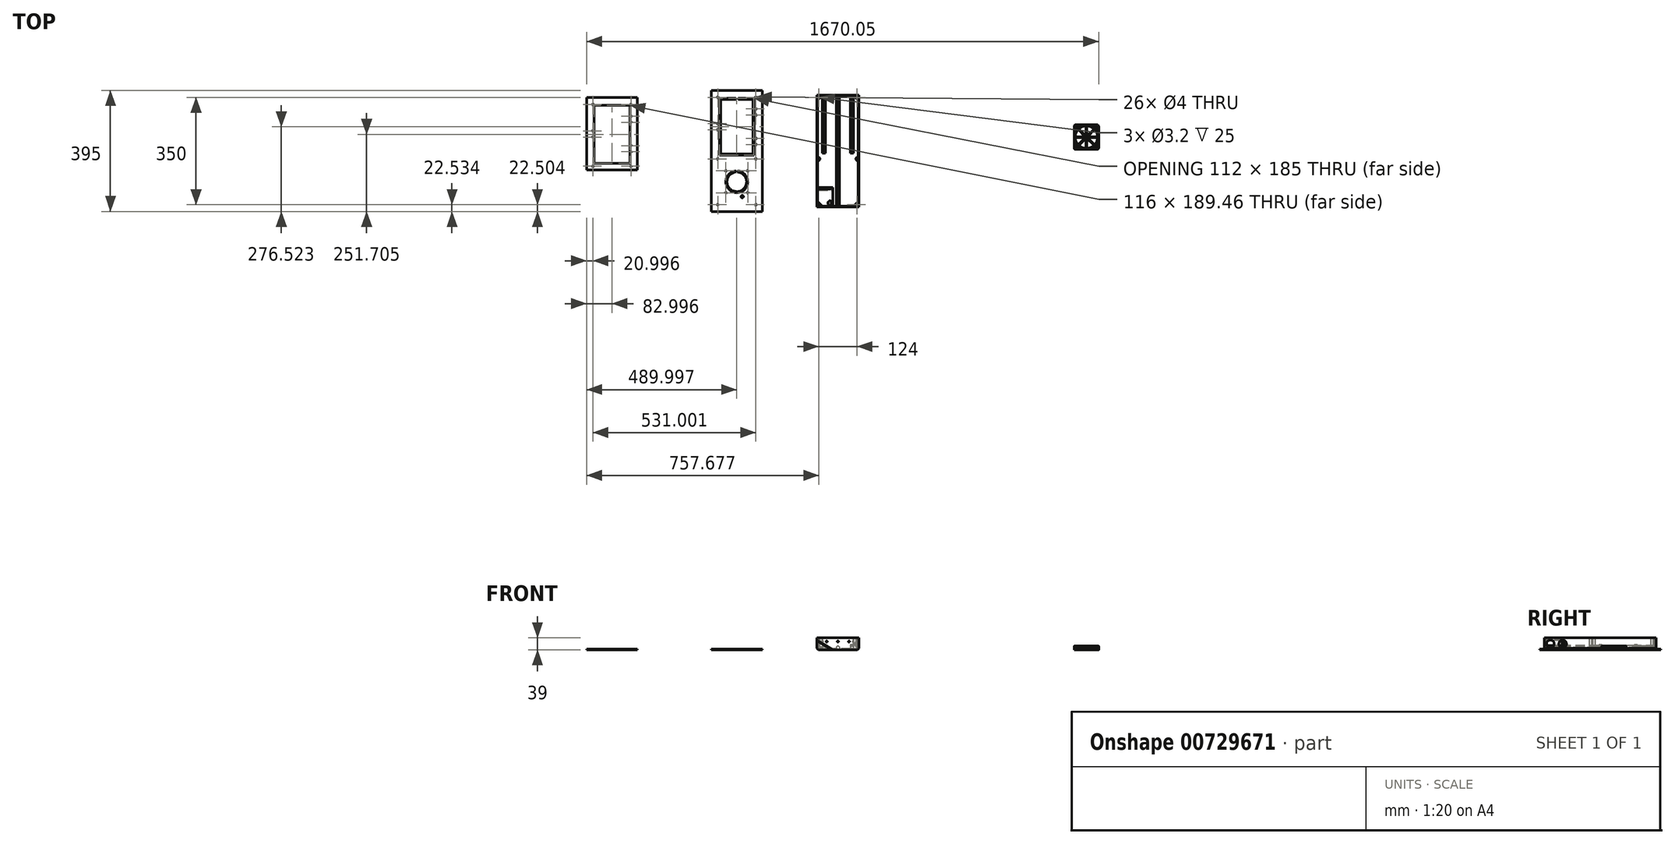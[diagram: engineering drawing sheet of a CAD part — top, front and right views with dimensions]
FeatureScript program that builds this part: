
annotation { "Feature Type Name" : "Feature", "Feature Type Description" : "" }
export const myFeature = defineFeature(function(context is Context, id is Id, definition is map)
    precondition{}
    {
        {
            var Q0;
            Q0=qCreatedBy(makeId("Top.planeOp"),FACE);
            var sketch = newSketch(context, id + "F0", { "sketchPlane" : qUnion([Q0])});
            skLineSegment(sketch, "E0.bottom", {"start": v(-453.37, 96.62) * mm, "end": v(-317.37, 96.62) * mm});
            skLineSegment(sketch, "E0.top", {"start": v(-453.37, -268.38) * mm, "end": v(-317.37, -268.38) * mm});
            skLineSegment(sketch, "E0.left", {"start": v(-453.37, 96.62) * mm, "end": v(-453.37, -268.38) * mm});
            skLineSegment(sketch, "E0.right", {"start": v(-317.37, 96.62) * mm, "end": v(-317.37, -268.38) * mm});
            skSolve(sketch);
        }
        {
            var Q0;
            Q0 = qSketchRegion(id + "F0", true);
            extrude(context, id + "F1", {"entities" : qUnion([Q0]), "depth" : 4 * mm, "offsetDistance" : 25 * mm});
        }
        {
            var Q0;
            Q0=makeQuery(id+"F1.opExtrude","CAP_FACE",FACE,{"disambiguationData":[OSD([sQuery(id+"F0.wireOp",EDGE,"E0.bottom"),sQuery(id+"F0.wireOp",EDGE,"E0.top"),sQuery(id+"F0.wireOp",EDGE,"E0.left"),sQuery(id+"F0.wireOp",EDGE,"E0.right")])],"isStart":false});
            var sketch = newSketch(context, id + "F2", { "sketchPlane" : qUnion([Q0])});
            skLineSegment(sketch, "E1.bottom", {"start": v(-453.37, 96.62) * mm, "end": v(-317.37, 96.62) * mm});
            skLineSegment(sketch, "E1.top", {"start": v(-453.37, -268.38) * mm, "end": v(-317.37, -268.38) * mm});
            skLineSegment(sketch, "E1.left", {"start": v(-453.37, 96.62) * mm, "end": v(-453.37, -268.38) * mm});
            skLineSegment(sketch, "E1.right", {"start": v(-317.37, 96.62) * mm, "end": v(-317.37, -268.38) * mm});
            skLineSegment(sketch, "E2.bottom", {"start": v(-319.87, -265.88) * mm, "end": v(-450.87, -265.88) * mm});
            skLineSegment(sketch, "E2.top", {"start": v(-319.87, 94.12) * mm, "end": v(-450.87, 94.12) * mm});
            skLineSegment(sketch, "E2.left", {"start": v(-319.87, -265.88) * mm, "end": v(-319.87, 94.12) * mm});
            skLineSegment(sketch, "E2.right", {"start": v(-450.87, -265.88) * mm, "end": v(-450.87, 94.12) * mm});
            skPoint(sketch, "E2.middle", {"position": v(-385.37, -85.88) * mm});
            skPoint(sketch, "E2.middle.positionSnap0", {"position": v(-385.37, 96.62) * mm});
            skPoint(sketch, "E2.middle.positionSnap1", {"position": v(-453.37, -85.88) * mm});
            skPoint(sketch, "E2.centerSnap0", {"position": v(-385.37, 96.62) * mm});
            skPoint(sketch, "E2.centerSnap1", {"position": v(-453.37, -85.88) * mm});
            skSolve(sketch);
        }
        {
            var Q0;
            Q0 = qSketchRegion(id + "F2", true);
            extrude(context, id + "F3", {"entities" : qUnion([Q0]), "operationType" : NewBodyOperationType.ADD, "depth" : 35 * mm, "offsetDistance" : 25 * mm});
        }
        {
            var Q0;
            Q0=makeQuery(id+"F1.opExtrude","CAP_FACE",FACE,{"disambiguationData":[OSD([sQuery(id+"F0.wireOp",EDGE,"E0.bottom"),sQuery(id+"F0.wireOp",EDGE,"E0.top"),sQuery(id+"F0.wireOp",EDGE,"E0.left"),sQuery(id+"F0.wireOp",EDGE,"E0.right")])],"isStart":false});
            var sketch = newSketch(context, id + "F4", { "sketchPlane" : qUnion([Q0])});
            skLineSegment(sketch, "E3", {"start": v(-385.37, 94.12) * mm, "end": v(-385.37, -265.88) * mm, "construction": true});
            skLineSegment(sketch, "E4.bottom", {"start": v(-450.87, 94.12) * mm, "end": v(-319.87, 94.12) * mm, "construction": true});
            skLineSegment(sketch, "E4.top", {"start": v(-450.87, 34.12) * mm, "end": v(-319.87, 34.12) * mm, "construction": true});
            skLineSegment(sketch, "E4.left", {"start": v(-450.87, 94.12) * mm, "end": v(-450.87, 34.12) * mm, "construction": true});
            skLineSegment(sketch, "E4.right", {"start": v(-319.87, 94.12) * mm, "end": v(-319.87, 34.12) * mm, "construction": true});
            skLineSegment(sketch, "E5.top", {"start": v(-450.87, -88.88) * mm, "end": v(-319.87, -88.88) * mm, "construction": true});
            skLineSegment(sketch, "E5.left", {"start": v(-450.87, 34.12) * mm, "end": v(-450.87, -88.88) * mm, "construction": true});
            skLineSegment(sketch, "E5.right", {"start": v(-319.87, 34.12) * mm, "end": v(-319.87, -88.88) * mm, "construction": true});
            skLineSegment(sketch, "E6.bottom", {"start": v(-339.37, -84.88) * mm, "end": v(-431.37, -84.88) * mm, "construction": true});
            skLineSegment(sketch, "E6.top", {"start": v(-339.37, 30.12) * mm, "end": v(-431.37, 30.12) * mm, "construction": true});
            skLineSegment(sketch, "E6.left", {"start": v(-339.37, -84.88) * mm, "end": v(-339.37, 30.12) * mm, "construction": true});
            skLineSegment(sketch, "E6.right", {"start": v(-431.37, -84.88) * mm, "end": v(-431.37, 30.12) * mm, "construction": true});
            skPoint(sketch, "E6.middle", {"position": v(-385.37, -27.38) * mm});
            skPoint(sketch, "E6.middle.positionSnap0", {"position": v(-450.87, -27.38) * mm});
            skPoint(sketch, "E6.centerSnap0", {"position": v(-450.87, -27.38) * mm});
            skCircle(sketch, "E7", {"center": v(-431.37, 30.12) * mm, "radius": 5 * mm});
            skCircle(sketch, "E8", {"center": v(-339.37, 30.12) * mm, "radius": 5 * mm});
            skCircle(sketch, "E9", {"center": v(-339.37, -84.88) * mm, "radius": 5 * mm});
            skCircle(sketch, "E10", {"center": v(-431.37, -84.88) * mm, "radius": 5 * mm});
            skCircle(sketch, "E11", {"center": v(-431.37, 30.12) * mm, "radius": 2 * mm});
            skCircle(sketch, "E12", {"center": v(-339.37, 30.12) * mm, "radius": 2 * mm});
            skCircle(sketch, "E13", {"center": v(-339.37, -84.88) * mm, "radius": 2 * mm});
            skCircle(sketch, "E14", {"center": v(-431.37, -84.88) * mm, "radius": 2 * mm});
            skLineSegment(sketch, "E15.top", {"start": v(-450.87, -218.88) * mm, "end": v(-319.87, -218.88) * mm, "construction": true});
            skLineSegment(sketch, "E15.left", {"start": v(-450.87, -88.88) * mm, "end": v(-450.87, -218.88) * mm, "construction": true});
            skLineSegment(sketch, "E15.right", {"start": v(-319.87, -88.88) * mm, "end": v(-319.87, -218.88) * mm, "construction": true});
            skLineSegment(sketch, "E16.bottom", {"start": v(-345.37, -193.88) * mm, "end": v(-425.37, -193.88) * mm, "construction": true});
            skLineSegment(sketch, "E16.top", {"start": v(-345.37, -113.88) * mm, "end": v(-425.37, -113.88) * mm, "construction": true});
            skLineSegment(sketch, "E16.left", {"start": v(-345.37, -193.88) * mm, "end": v(-345.37, -113.88) * mm, "construction": true});
            skLineSegment(sketch, "E16.right", {"start": v(-425.37, -193.88) * mm, "end": v(-425.37, -113.88) * mm, "construction": true});
            skPoint(sketch, "E16.middle", {"position": v(-385.37, -153.88) * mm});
            skPoint(sketch, "E16.middle.positionSnap0", {"position": v(-450.87, -153.88) * mm});
            skPoint(sketch, "E16.centerSnap0", {"position": v(-450.87, -153.88) * mm});
            skLineSegment(sketch, "E17.top", {"start": v(-450.87, -265.88) * mm, "end": v(-319.87, -265.88) * mm, "construction": true});
            skLineSegment(sketch, "E17.left", {"start": v(-450.87, -218.88) * mm, "end": v(-450.87, -265.88) * mm, "construction": true});
            skLineSegment(sketch, "E17.right", {"start": v(-319.87, -218.88) * mm, "end": v(-319.87, -265.88) * mm, "construction": true});
            skLineSegment(sketch, "E18.bottom", {"start": v(-349.62, -189.63) * mm, "end": v(-421.12, -189.63) * mm, "construction": true});
            skLineSegment(sketch, "E18.top", {"start": v(-349.62, -118.13) * mm, "end": v(-421.12, -118.13) * mm, "construction": true});
            skLineSegment(sketch, "E18.left", {"start": v(-349.62, -189.63) * mm, "end": v(-349.62, -118.13) * mm, "construction": true});
            skLineSegment(sketch, "E18.right", {"start": v(-421.12, -189.63) * mm, "end": v(-421.12, -118.13) * mm, "construction": true});
            skSolve(sketch);
        }
        {
            var Q0;
            Q0 = qSketchRegion(id + "F4", true);
            extrude(context, id + "F5", {"entities" : qUnion([Q0]), "operationType" : NewBodyOperationType.ADD, "depth" : 12 * mm, "offsetDistance" : 25 * mm});
        }
        {
            var Q0;
            Q0=makeQuery(id+"F3.boolean.opBoolean","MERGE",FACE,{"derivedFrom":[makeQuery(id+"F1.opExtrude","SWEPT_FACE",FACE,{"disambiguationData":[OSD([sQuery(id+"F0.wireOp",EDGE,"E0.top")])]}),makeQuery(id+"F3.opExtrude","SWEPT_FACE",FACE,{"disambiguationData":[OSD([sQuery(id+"F2.wireOp",EDGE,"E1.top")])]})]});
            var sketch = newSketch(context, id + "F6", { "sketchPlane" : qUnion([Q0])});
            skLineSegment(sketch, "E19", {"start": v(-453.37, 0) * mm, "end": v(-453.37, 30) * mm});
            skLineSegment(sketch, "E20", {"start": v(-453.37, 30) * mm, "end": v(-403.37, 0) * mm});
            skLineSegment(sketch, "E21", {"start": v(-403.37, 0) * mm, "end": v(-453.37, 0) * mm});
            skSolve(sketch);
        }
        {
            var Q0;
            Q0 = qSketchRegion(id + "F6", true);
            extrude(context, id + "F7", {"entities" : qUnion([Q0]), "operationType" : NewBodyOperationType.REMOVE, "oppositeDirection" : true, "depth" : 59 * mm, "offsetDistance" : 25 * mm});
        }
        {
            var Q0;
            Q0=makeQuery(id+"F7.boolean.opBoolean","COPY",FACE,{"derivedFrom":makeQuery(id+"F7.opExtrude","SWEPT_FACE",FACE,{"disambiguationData":[OSD([sQuery(id+"F6.wireOp",EDGE,"E20")])]})});
            var sketch = newSketch(context, id + "F8", { "sketchPlane" : qUnion([Q0])});
            skLineSegment(sketch, "E22.bottom", {"start": v(-404.2, 268.38) * mm, "end": v(-345.89, 268.38) * mm});
            skLineSegment(sketch, "E22.top", {"start": v(-404.2, 209.38) * mm, "end": v(-345.89, 209.38) * mm});
            skLineSegment(sketch, "E22.left", {"start": v(-404.2, 268.38) * mm, "end": v(-404.2, 209.38) * mm});
            skLineSegment(sketch, "E22.right", {"start": v(-345.89, 268.38) * mm, "end": v(-345.89, 209.38) * mm});
            skSolve(sketch);
        }
        {
            var Q0;
            Q0 = qSketchRegion(id + "F8", true);
            extrude(context, id + "F9", {"entities" : qUnion([Q0]), "operationType" : NewBodyOperationType.ADD, "oppositeDirection" : true, "depth" : 4 * mm, "offsetDistance" : 25 * mm});
        }
        {
            var Q0;
            Q0=makeQuery(id+"F7.boolean.opBoolean","COPY",FACE,{"derivedFrom":makeQuery(id+"F7.opExtrude","CAP_FACE",FACE,{"disambiguationData":[OSD([sQuery(id+"F6.wireOp",EDGE,"E19"),sQuery(id+"F6.wireOp",EDGE,"E20"),sQuery(id+"F6.wireOp",EDGE,"E21")])],"isStart":false})});
            var sketch = newSketch(context, id + "F10", { "sketchPlane" : qUnion([Q0])});
            skLineSegment(sketch, "E23", {"start": v(-453.37, 0) * mm, "end": v(-453.37, 30) * mm});
            skLineSegment(sketch, "E24", {"start": v(-453.37, 30) * mm, "end": v(-403.37, 0) * mm});
            skLineSegment(sketch, "E25", {"start": v(-403.37, 0) * mm, "end": v(-453.37, 0) * mm});
            skSolve(sketch);
        }
        {
            var Q0;
            Q0 = qSketchRegion(id + "F10", true);
            extrude(context, id + "F11", {"entities" : qUnion([Q0]), "operationType" : NewBodyOperationType.ADD, "depth" : 4 * mm, "offsetDistance" : 25 * mm});
        }
        {
            var Q0;
            Q0=makeQuery(id+"F3.boolean.opBoolean","MERGE",FACE,{"derivedFrom":[makeQuery(id+"F1.opExtrude","SWEPT_FACE",FACE,{"disambiguationData":[OSD([sQuery(id+"F0.wireOp",EDGE,"E0.right")])]}),makeQuery(id+"F3.opExtrude","SWEPT_FACE",FACE,{"disambiguationData":[OSD([sQuery(id+"F2.wireOp",EDGE,"E1.right")])]})]});
            var sketch = newSketch(context, id + "F12", { "sketchPlane" : qUnion([Q0])});
            skLineSegment(sketch, "E26", {"start": v(-268.38, 19.5) * mm, "end": v(96.62, 19.5) * mm, "construction": true});
            skCircle(sketch, "E27", {"center": v(-248.38, 19.5) * mm, "radius": 12.5 * mm});
            skCircle(sketch, "E28", {"center": v(-208.38, 19.5) * mm, "radius": 12.5 * mm});
            skLineSegment(sketch, "E29", {"start": v(-248.38, 19.5) * mm, "end": v(-268.38, 19.5) * mm, "construction": true});
            skLineSegment(sketch, "E30", {"start": v(-248.38, 19.5) * mm, "end": v(-208.38, 19.5) * mm, "construction": true});
            skSolve(sketch);
        }
        {
            var Q0;
            Q0 = qSketchRegion(id + "F12", true);
            extrude(context, id + "F13", {"entities" : qUnion([Q0]), "operationType" : NewBodyOperationType.REMOVE, "oppositeDirection" : true, "depth" : 25 * mm, "offsetDistance" : 25 * mm});
        }
        {
            var Q0;
            Q0=makeQuery(id+"F9.boolean.opBoolean","MERGE",FACE,{"derivedFrom":[makeQuery(id+"F7.boolean.opBoolean","COPY",FACE,{"derivedFrom":makeQuery(id+"F7.opExtrude","SWEPT_FACE",FACE,{"disambiguationData":[OSD([sQuery(id+"F6.wireOp",EDGE,"E20")])]})}),makeQuery(id+"F9.opExtrude","CAP_FACE",FACE,{"disambiguationData":[OSD([sQuery(id+"F8.wireOp",EDGE,"E22.bottom"),sQuery(id+"F8.wireOp",EDGE,"E22.top"),sQuery(id+"F8.wireOp",EDGE,"E22.left"),sQuery(id+"F8.wireOp",EDGE,"E22.right")])],"isStart":true})]});
            var sketch = newSketch(context, id + "F14", { "sketchPlane" : qUnion([Q0])});
            skLineSegment(sketch, "E31.bottom", {"start": v(-345.89, 268.38) * mm, "end": v(-404.2, 268.38) * mm, "construction": true});
            skLineSegment(sketch, "E31.top", {"start": v(-345.89, 243.38) * mm, "end": v(-404.2, 243.38) * mm, "construction": true});
            skLineSegment(sketch, "E31.left", {"start": v(-345.89, 268.38) * mm, "end": v(-345.89, 243.38) * mm, "construction": true});
            skLineSegment(sketch, "E31.right", {"start": v(-404.2, 268.38) * mm, "end": v(-404.2, 243.38) * mm, "construction": true});
            skLineSegment(sketch, "E32", {"start": v(-404.2, 255.88) * mm, "end": v(-345.89, 255.88) * mm, "construction": true});
            skCircle(sketch, "E33", {"center": v(-357.32, 255.88) * mm, "radius": 7.47 * mm});
            skSolve(sketch);
        }
        {
            var Q0;
            Q0=makeQuery(id+"F14.imprint","IMPRINT",FACE,{"disambiguationData":[TD([[makeQuery(id+"F14.imprint","IMPRINT",EDGE,{"derivedFrom":sQuery(id+"F14.wireOp",EDGE,"E33")}),1.0]])]});
            var Q1;
            Q1=sQuery(id+"F14.wireOp",EDGE,"E33");
            extrude(context, id + "F15", {"entities" : qUnion([Q0]), "operationType" : NewBodyOperationType.REMOVE, "surfaceEntities" : qUnion([Q1]), "oppositeDirection" : true, "depth" : 25 * mm, "offsetDistance" : 25 * mm});
        }
        {
            var Q0;
            Q0=makeQuery(id+"F5.boolean.opBoolean","SPLIT",FACE,{"disambiguationData":[TD([makeQuery(id+"F3.opExtrude","SWEPT_FACE",FACE,{"disambiguationData":[OSD([sQuery(id+"F2.wireOp",EDGE,"E2.bottom")])]})])],"derivedFrom":makeQuery(id+"F1.opExtrude","CAP_FACE",FACE,{"disambiguationData":[OSD([sQuery(id+"F0.wireOp",EDGE,"E0.bottom"),sQuery(id+"F0.wireOp",EDGE,"E0.top"),sQuery(id+"F0.wireOp",EDGE,"E0.left"),sQuery(id+"F0.wireOp",EDGE,"E0.right")])],"isStart":false})});
            var sketch = newSketch(context, id + "F16", { "sketchPlane" : qUnion([Q0])});
            skLineSegment(sketch, "E34.top", {"start": v(-436.34, 94.12) * mm, "end": v(-426.34, 94.12) * mm});
            skLineSegment(sketch, "E34.left", {"start": v(-436.34, 30.7) * mm, "end": v(-436.34, 94.12) * mm});
            skLineSegment(sketch, "E34.right", {"start": v(-426.34, 30.7) * mm, "end": v(-426.34, 94.12) * mm});
            skLineSegment(sketch, "E35.top", {"start": v(-344.35, 94.12) * mm, "end": v(-334.35, 94.12) * mm});
            skLineSegment(sketch, "E35.left", {"start": v(-344.35, 30.56) * mm, "end": v(-344.35, 94.12) * mm});
            skLineSegment(sketch, "E35.right", {"start": v(-334.35, 30.56) * mm, "end": v(-334.35, 94.12) * mm});
            skLineSegment(sketch, "E36.top", {"start": v(-436.34, -93.27) * mm, "end": v(-426.34, -93.27) * mm});
            skLineSegment(sketch, "E36.left", {"start": v(-436.34, 30.7) * mm, "end": v(-436.34, -93.27) * mm});
            skLineSegment(sketch, "E36.right", {"start": v(-426.34, 30.7) * mm, "end": v(-426.34, -93.27) * mm});
            skLineSegment(sketch, "E37.top", {"start": v(-344.35, -93.27) * mm, "end": v(-334.35, -93.27) * mm});
            skLineSegment(sketch, "E37.left", {"start": v(-344.35, 30.56) * mm, "end": v(-344.35, -93.27) * mm});
            skLineSegment(sketch, "E37.right", {"start": v(-334.35, 30.56) * mm, "end": v(-334.35, -93.27) * mm});
            skLineSegment(sketch, "E38.bottom", {"start": v(-385.37, 94.12) * mm, "end": v(-380.37, 94.12) * mm});
            skLineSegment(sketch, "E38.top", {"start": v(-385.37, -265.88) * mm, "end": v(-380.37, -265.88) * mm});
            skLineSegment(sketch, "E38.left", {"start": v(-385.37, 94.12) * mm, "end": v(-385.37, -265.88) * mm});
            skLineSegment(sketch, "E38.right", {"start": v(-380.37, 94.12) * mm, "end": v(-380.37, -265.88) * mm});
            skLineSegment(sketch, "E39.MirrorCS", {"start": v(-390.37, 94.12) * mm, "end": v(-390.37, -265.88) * mm});
            skLineSegment(sketch, "E40.MirrorCS", {"start": v(-385.37, -265.88) * mm, "end": v(-390.37, -265.88) * mm});
            skLineSegment(sketch, "E41.MirrorCS", {"start": v(-385.37, 94.12) * mm, "end": v(-390.37, 94.12) * mm});
            skSolve(sketch);
        }
        {
            var Q0;
            Q0 = qSketchRegion(id + "F16", true);
            extrude(context, id + "F17", {"entities" : qUnion([Q0]), "operationType" : NewBodyOperationType.ADD, "depth" : 10 * mm, "offsetDistance" : 25 * mm});
        }
        {
            var Q0;
            Q0=makeQuery(id+"F17.opExtrude","CAP_EDGE",EDGE,{"disambiguationData":[OSD([sQuery(id+"F16.wireOp",EDGE,"E38.right")])],"isStart":false});
            var Q1;
            Q1=makeQuery(id+"F17.opExtrude","CAP_EDGE",EDGE,{"disambiguationData":[OSD([sQuery(id+"F16.wireOp",EDGE,"E39.MirrorCS")])],"isStart":false});
            var Q2;
            {var subQ0=sQuery(id+"F16.wireOp",EDGE,"E37.left");var subQ1=sQuery(id+"F16.wireOp",EDGE,"E35.left");Q2=makeQuery(id+"F17.boolean.opBoolean","SPLIT",EDGE,{"disambiguationData":[TD([makeQuery(id+"F5.opExtrude","SWEPT_FACE",FACE,{"disambiguationData":[OSD([sQuery(id+"F4.wireOp",EDGE,"E8")])]}),makeQuery(id+"F5.opExtrude","SWEPT_FACE",FACE,{"disambiguationData":[OSD([sQuery(id+"F4.wireOp",EDGE,"E9")])]}),makeQuery(id+"F17.opExtrude","CAP_FACE",FACE,{"disambiguationData":[OSD([sQuery(id+"F16.wireOp",EDGE,"E35.top"),subQ1,sQuery(id+"F16.wireOp",EDGE,"E35.right"),sQuery(id+"F16.wireOp",EDGE,"E37.top"),subQ0,sQuery(id+"F16.wireOp",EDGE,"E37.right")])],"isStart":false}),makeQuery(id+"F17.opExtrude","SWEPT_FACE",FACE,{"disambiguationData":[OSD([subQ1,subQ0])]})])],"derivedFrom":makeQuery(id+"F17.opExtrude","CAP_EDGE",EDGE,{"disambiguationData":[OSD([subQ1,subQ0])],"isStart":false})});}
            var Q3;
            Q3=makeQuery(id+"F17.opExtrude","CAP_EDGE",EDGE,{"disambiguationData":[OSD([sQuery(id+"F16.wireOp",EDGE,"E35.right"),sQuery(id+"F16.wireOp",EDGE,"E37.right")])],"isStart":false});
            var Q4;
            {var subQ0=sQuery(id+"F16.wireOp",EDGE,"E37.left");var subQ1=sQuery(id+"F16.wireOp",EDGE,"E37.top");var subQ2=sQuery(id+"F16.wireOp",EDGE,"E35.left");Q4=makeQuery(id+"F17.boolean.opBoolean","SPLIT",EDGE,{"disambiguationData":[TD([makeQuery(id+"F5.opExtrude","SWEPT_FACE",FACE,{"disambiguationData":[OSD([sQuery(id+"F4.wireOp",EDGE,"E9")])]}),makeQuery(id+"F17.opExtrude","CAP_FACE",FACE,{"disambiguationData":[OSD([sQuery(id+"F16.wireOp",EDGE,"E35.top"),subQ2,sQuery(id+"F16.wireOp",EDGE,"E35.right"),subQ1,subQ0,sQuery(id+"F16.wireOp",EDGE,"E37.right")])],"isStart":false}),makeQuery(id+"F17.opExtrude","SWEPT_FACE",FACE,{"disambiguationData":[OSD([subQ2,subQ0])]}),makeQuery(id+"F17.opExtrude","SWEPT_FACE",FACE,{"disambiguationData":[OSD([subQ1])]})])],"derivedFrom":makeQuery(id+"F17.opExtrude","CAP_EDGE",EDGE,{"disambiguationData":[OSD([subQ2,subQ0])],"isStart":false})});}
            var Q5;
            {var subQ0=sQuery(id+"F16.wireOp",EDGE,"E37.left");var subQ1=sQuery(id+"F16.wireOp",EDGE,"E35.left");Q5=makeQuery(id+"F17.boolean.opBoolean","SPLIT",EDGE,{"disambiguationData":[TD([makeQuery(id+"F3.opExtrude","SWEPT_FACE",FACE,{"disambiguationData":[OSD([sQuery(id+"F2.wireOp",EDGE,"E2.top")])]}),makeQuery(id+"F5.opExtrude","SWEPT_FACE",FACE,{"disambiguationData":[OSD([sQuery(id+"F4.wireOp",EDGE,"E8")])]}),makeQuery(id+"F17.opExtrude","CAP_FACE",FACE,{"disambiguationData":[OSD([sQuery(id+"F16.wireOp",EDGE,"E35.top"),subQ1,sQuery(id+"F16.wireOp",EDGE,"E35.right"),sQuery(id+"F16.wireOp",EDGE,"E37.top"),subQ0,sQuery(id+"F16.wireOp",EDGE,"E37.right")])],"isStart":false}),makeQuery(id+"F17.opExtrude","SWEPT_FACE",FACE,{"disambiguationData":[OSD([subQ1,subQ0])]})])],"derivedFrom":makeQuery(id+"F17.opExtrude","CAP_EDGE",EDGE,{"disambiguationData":[OSD([subQ1,subQ0])],"isStart":false})});}
            var Q6;
            Q6=makeQuery(id+"F17.opExtrude","CAP_EDGE",EDGE,{"disambiguationData":[OSD([sQuery(id+"F16.wireOp",EDGE,"E34.right"),sQuery(id+"F16.wireOp",EDGE,"E36.right")])],"isStart":false});
            var Q7;
            {var subQ0=sQuery(id+"F16.wireOp",EDGE,"E36.left");var subQ1=sQuery(id+"F16.wireOp",EDGE,"E34.left");Q7=makeQuery(id+"F17.boolean.opBoolean","SPLIT",EDGE,{"disambiguationData":[TD([makeQuery(id+"F3.opExtrude","SWEPT_FACE",FACE,{"disambiguationData":[OSD([sQuery(id+"F2.wireOp",EDGE,"E2.top")])]}),makeQuery(id+"F5.opExtrude","SWEPT_FACE",FACE,{"disambiguationData":[OSD([sQuery(id+"F4.wireOp",EDGE,"E7")])]}),makeQuery(id+"F17.opExtrude","CAP_FACE",FACE,{"disambiguationData":[OSD([sQuery(id+"F16.wireOp",EDGE,"E34.top"),subQ1,sQuery(id+"F16.wireOp",EDGE,"E34.right"),sQuery(id+"F16.wireOp",EDGE,"E36.top"),subQ0,sQuery(id+"F16.wireOp",EDGE,"E36.right")])],"isStart":false}),makeQuery(id+"F17.opExtrude","SWEPT_FACE",FACE,{"disambiguationData":[OSD([subQ1,subQ0])]})])],"derivedFrom":makeQuery(id+"F17.opExtrude","CAP_EDGE",EDGE,{"disambiguationData":[OSD([subQ1,subQ0])],"isStart":false})});}
            var Q8;
            {var subQ0=sQuery(id+"F16.wireOp",EDGE,"E36.left");var subQ1=sQuery(id+"F16.wireOp",EDGE,"E34.left");Q8=makeQuery(id+"F17.boolean.opBoolean","SPLIT",EDGE,{"disambiguationData":[TD([makeQuery(id+"F5.opExtrude","SWEPT_FACE",FACE,{"disambiguationData":[OSD([sQuery(id+"F4.wireOp",EDGE,"E7")])]}),makeQuery(id+"F5.opExtrude","SWEPT_FACE",FACE,{"disambiguationData":[OSD([sQuery(id+"F4.wireOp",EDGE,"E10")])]}),makeQuery(id+"F17.opExtrude","CAP_FACE",FACE,{"disambiguationData":[OSD([sQuery(id+"F16.wireOp",EDGE,"E34.top"),subQ1,sQuery(id+"F16.wireOp",EDGE,"E34.right"),sQuery(id+"F16.wireOp",EDGE,"E36.top"),subQ0,sQuery(id+"F16.wireOp",EDGE,"E36.right")])],"isStart":false}),makeQuery(id+"F17.opExtrude","SWEPT_FACE",FACE,{"disambiguationData":[OSD([subQ1,subQ0])]})])],"derivedFrom":makeQuery(id+"F17.opExtrude","CAP_EDGE",EDGE,{"disambiguationData":[OSD([subQ1,subQ0])],"isStart":false})});}
            var Q9;
            {var subQ0=sQuery(id+"F16.wireOp",EDGE,"E36.top");var subQ1=sQuery(id+"F16.wireOp",EDGE,"E36.left");var subQ2=sQuery(id+"F16.wireOp",EDGE,"E34.left");Q9=makeQuery(id+"F17.boolean.opBoolean","SPLIT",EDGE,{"disambiguationData":[TD([makeQuery(id+"F5.opExtrude","SWEPT_FACE",FACE,{"disambiguationData":[OSD([sQuery(id+"F4.wireOp",EDGE,"E10")])]}),makeQuery(id+"F17.opExtrude","CAP_FACE",FACE,{"disambiguationData":[OSD([sQuery(id+"F16.wireOp",EDGE,"E34.top"),subQ2,sQuery(id+"F16.wireOp",EDGE,"E34.right"),subQ0,subQ1,sQuery(id+"F16.wireOp",EDGE,"E36.right")])],"isStart":false}),makeQuery(id+"F17.opExtrude","SWEPT_FACE",FACE,{"disambiguationData":[OSD([subQ2,subQ1])]}),makeQuery(id+"F17.opExtrude","SWEPT_FACE",FACE,{"disambiguationData":[OSD([subQ0])]})])],"derivedFrom":makeQuery(id+"F17.opExtrude","CAP_EDGE",EDGE,{"disambiguationData":[OSD([subQ2,subQ1])],"isStart":false})});}
            var Q10;
            Q10=makeQuery(id+"F3.opExtrude","CAP_EDGE",EDGE,{"disambiguationData":[OSD([sQuery(id+"F2.wireOp",EDGE,"E2.left")])],"isStart":true});
            var Q11;
            Q11=makeQuery(id+"F3.opExtrude","CAP_EDGE",EDGE,{"disambiguationData":[OSD([sQuery(id+"F2.wireOp",EDGE,"E2.right")])],"isStart":true});
            var Q12;
            {var subQ0=sQuery(id+"F2.wireOp",EDGE,"E2.top");Q12=makeQuery(id+"F17.boolean.opBoolean","SPLIT",EDGE,{"disambiguationData":[TD([makeQuery(id+"F17.opExtrude","SWEPT_FACE",FACE,{"disambiguationData":[OSD([sQuery(id+"F16.wireOp",EDGE,"E39.MirrorCS")])]})])],"derivedFrom":makeQuery(id+"F3.opExtrude","CAP_EDGE",EDGE,{"disambiguationData":[OSD([subQ0])],"isStart":true})});}
            var Q13;
            {var subQ0=sQuery(id+"F2.wireOp",EDGE,"E2.top");Q13=makeQuery(id+"F17.boolean.opBoolean","SPLIT",EDGE,{"disambiguationData":[TD([makeQuery(id+"F17.opExtrude","SWEPT_FACE",FACE,{"disambiguationData":[OSD([sQuery(id+"F16.wireOp",EDGE,"E38.right")])]})])],"derivedFrom":makeQuery(id+"F3.opExtrude","CAP_EDGE",EDGE,{"disambiguationData":[OSD([subQ0])],"isStart":true})});}
            var Q14;
            {var subQ0=sQuery(id+"F2.wireOp",EDGE,"E2.top");Q14=makeQuery(id+"F17.boolean.opBoolean","SPLIT",EDGE,{"disambiguationData":[TD([makeQuery(id+"F3.opExtrude","SWEPT_FACE",FACE,{"disambiguationData":[OSD([sQuery(id+"F2.wireOp",EDGE,"E2.right")])]})])],"derivedFrom":makeQuery(id+"F3.opExtrude","CAP_EDGE",EDGE,{"disambiguationData":[OSD([subQ0])],"isStart":true})});}
            var Q15;
            {var subQ0=sQuery(id+"F2.wireOp",EDGE,"E2.top");Q15=makeQuery(id+"F17.boolean.opBoolean","SPLIT",EDGE,{"disambiguationData":[TD([makeQuery(id+"F3.opExtrude","SWEPT_FACE",FACE,{"disambiguationData":[OSD([sQuery(id+"F2.wireOp",EDGE,"E2.left")])]})])],"derivedFrom":makeQuery(id+"F3.opExtrude","CAP_EDGE",EDGE,{"disambiguationData":[OSD([subQ0])],"isStart":true})});}
            var Q16;
            {var subQ0=sQuery(id+"F2.wireOp",EDGE,"E2.bottom");Q16=makeQuery(id+"F17.boolean.opBoolean","SPLIT",EDGE,{"disambiguationData":[TD([makeQuery(id+"F3.opExtrude","SWEPT_FACE",FACE,{"disambiguationData":[OSD([sQuery(id+"F2.wireOp",EDGE,"E2.left")])]})])],"derivedFrom":makeQuery(id+"F3.opExtrude","CAP_EDGE",EDGE,{"disambiguationData":[OSD([subQ0])],"isStart":true})});}
            var Q17;
            {var subQ0=sQuery(id+"F2.wireOp",EDGE,"E2.bottom");Q17=makeQuery(id+"F17.boolean.opBoolean","SPLIT",EDGE,{"disambiguationData":[TD([makeQuery(id+"F17.opExtrude","SWEPT_FACE",FACE,{"disambiguationData":[OSD([sQuery(id+"F16.wireOp",EDGE,"E39.MirrorCS")])]})])],"derivedFrom":makeQuery(id+"F3.opExtrude","CAP_EDGE",EDGE,{"disambiguationData":[OSD([subQ0])],"isStart":true})});}
            var Q18;
            {var subQ0=makeQuery(id+"F5.boolean.opBoolean","SPLIT",FACE,{"disambiguationData":[TD([makeQuery(id+"F3.opExtrude","SWEPT_FACE",FACE,{"disambiguationData":[OSD([sQuery(id+"F2.wireOp",EDGE,"E2.bottom")])]})])],"derivedFrom":makeQuery(id+"F1.opExtrude","CAP_FACE",FACE,{"disambiguationData":[OSD([sQuery(id+"F0.wireOp",EDGE,"E0.bottom"),sQuery(id+"F0.wireOp",EDGE,"E0.top"),sQuery(id+"F0.wireOp",EDGE,"E0.left"),sQuery(id+"F0.wireOp",EDGE,"E0.right")])],"isStart":false})});Q18=makeQuery(id+"F11.boolean.opBoolean","MERGE",EDGE,{"derivedFrom":[makeQuery(id+"F7.boolean.opBoolean","INTERSECT",EDGE,{"derivedFrom":[subQ0,makeQuery(id+"F7.opExtrude","CAP_FACE",FACE,{"disambiguationData":[OSD([sQuery(id+"F6.wireOp",EDGE,"E19"),sQuery(id+"F6.wireOp",EDGE,"E20"),sQuery(id+"F6.wireOp",EDGE,"E21")])],"isStart":false})]}),makeQuery(id+"F9.boolean.opBoolean","INTERSECT",EDGE,{"derivedFrom":[subQ0,makeQuery(id+"F9.opExtrude","SWEPT_FACE",FACE,{"disambiguationData":[OSD([sQuery(id+"F8.wireOp",EDGE,"E22.top")])]})]})]});}
            var Q19;
            Q19=makeQuery(id+"F11.boolean.opBoolean","MERGE",EDGE,{"derivedFrom":[makeQuery(id+"F1.opExtrude","CAP_EDGE",EDGE,{"disambiguationData":[OSD([sQuery(id+"F0.wireOp",EDGE,"E0.left")])],"isStart":true}),makeQuery(id+"F11.opExtrude","SWEPT_EDGE",EDGE,{"disambiguationData":[OSD([sQuery(id+"F10.wireOp",EDGE,"E23"),sQuery(id+"F10.wireOp",EDGE,"E25")])]})]});
            var Q20;
            Q20=makeQuery(id+"F1.opExtrude","CAP_EDGE",EDGE,{"disambiguationData":[OSD([sQuery(id+"F0.wireOp",EDGE,"E0.right")])],"isStart":true});
            var Q21;
            {var subQ0=makeQuery(id+"F3.opExtrude","SWEPT_FACE",FACE,{"disambiguationData":[OSD([sQuery(id+"F2.wireOp",EDGE,"E2.right")])]});Q21=makeQuery(id+"F11.boolean.opBoolean","MERGE",EDGE,{"derivedFrom":[makeQuery(id+"F7.boolean.opBoolean","INTERSECT",EDGE,{"derivedFrom":[subQ0,makeQuery(id+"F7.opExtrude","CAP_FACE",FACE,{"disambiguationData":[OSD([sQuery(id+"F6.wireOp",EDGE,"E19"),sQuery(id+"F6.wireOp",EDGE,"E20"),sQuery(id+"F6.wireOp",EDGE,"E21")])],"isStart":false})]}),makeQuery(id+"F9.boolean.opBoolean","INTERSECT",EDGE,{"derivedFrom":[subQ0,makeQuery(id+"F9.opExtrude","SWEPT_FACE",FACE,{"disambiguationData":[OSD([sQuery(id+"F8.wireOp",EDGE,"E22.top")])]})]})]});}
            chamfer(context, id + "F18", {"entities" : qUnion([Q0, Q1, Q2, Q3, Q4, Q5, Q6, Q7, Q8, Q9, Q10, Q11, Q12, Q13, Q14, Q15, Q16, Q17, Q18, Q19, Q20, Q21]), "width" : 5 * mm, "tangentPropagation" : true});
        }
        {
            var Q0;
            Q0=makeQuery(id+"F3.opExtrude","SWEPT_FACE",FACE,{"disambiguationData":[OSD([sQuery(id+"F2.wireOp",EDGE,"E2.top")])]});
            var sketch = newSketch(context, id + "F19", { "sketchPlane" : qUnion([Q0])});
            skLineSegment(sketch, "E42.bottom", {"start": v(-319.87, 39) * mm, "end": v(-450.87, 39) * mm, "construction": true});
            skLineSegment(sketch, "E42.top", {"start": v(-319.87, 15) * mm, "end": v(-450.87, 15) * mm, "construction": true});
            skLineSegment(sketch, "E42.left", {"start": v(-319.87, 39) * mm, "end": v(-319.87, 15) * mm, "construction": true});
            skLineSegment(sketch, "E42.right", {"start": v(-450.87, 39) * mm, "end": v(-450.87, 15) * mm, "construction": true});
            skLineSegment(sketch, "E43", {"start": v(-319.87, 27) * mm, "end": v(-450.87, 27) * mm, "construction": true});
            skLineSegment(sketch, "E44", {"start": v(-385.37, 14) * mm, "end": v(-385.37, 39) * mm, "construction": true});
            skCircle(sketch, "E45", {"center": v(-335.98, 27) * mm, "radius": 2 * mm});
            skCircle(sketch, "E46", {"center": v(-385.37, 27) * mm, "radius": 2 * mm});
            skCircle(sketch, "E47.MirrorC", {"center": v(-434.76, 27) * mm, "radius": 2 * mm});
            skSolve(sketch);
        }
        {
            var Q0;
            Q0 = qSketchRegion(id + "F19", true);
            extrude(context, id + "F20", {"entities" : qUnion([Q0]), "operationType" : NewBodyOperationType.REMOVE, "oppositeDirection" : true, "depth" : 25 * mm, "offsetDistance" : 25 * mm});
        }
        {
            var Q0;
            Q0=makeQuery(id+"F3.opExtrude","SWEPT_FACE",FACE,{"disambiguationData":[OSD([sQuery(id+"F2.wireOp",EDGE,"E2.bottom")])]});
            var sketch = newSketch(context, id + "F21", { "sketchPlane" : qUnion([Q0])});
            skLineSegment(sketch, "E48.bottom", {"start": v(319.87, 39) * mm, "end": v(450.87, 39) * mm, "construction": true});
            skLineSegment(sketch, "E48.top", {"start": v(319.87, 15) * mm, "end": v(450.87, 15) * mm, "construction": true});
            skLineSegment(sketch, "E48.left", {"start": v(319.87, 39) * mm, "end": v(319.87, 15) * mm, "construction": true});
            skLineSegment(sketch, "E48.right", {"start": v(450.87, 39) * mm, "end": v(450.87, 15) * mm, "construction": true});
            skLineSegment(sketch, "E49", {"start": v(319.87, 27) * mm, "end": v(450.87, 27) * mm, "construction": true});
            skLineSegment(sketch, "E50", {"start": v(385.37, 15) * mm, "end": v(385.37, 39) * mm, "construction": true});
            skCircle(sketch, "E51", {"center": v(348.81, 27) * mm, "radius": 2 * mm});
            skCircle(sketch, "E52", {"center": v(385.37, 27) * mm, "radius": 2 * mm});
            skCircle(sketch, "E53.MirrorC", {"center": v(421.93, 27) * mm, "radius": 2 * mm});
            skSolve(sketch);
        }
        {
            var Q0;
            Q0 = qSketchRegion(id + "F21", true);
            extrude(context, id + "F22", {"entities" : qUnion([Q0]), "operationType" : NewBodyOperationType.REMOVE, "oppositeDirection" : true, "depth" : 25 * mm, "offsetDistance" : 25 * mm});
        }
        {
            var Q0;
            Q0=makeQuery(id+"F3.opExtrude","SWEPT_EDGE",EDGE,{"disambiguationData":[OSD([sQuery(id+"F2.wireOp",EDGE,"E2.top"),sQuery(id+"F2.wireOp",EDGE,"E2.left")])]});
            var Q1;
            Q1=makeQuery(id+"F3.opExtrude","SWEPT_EDGE",EDGE,{"disambiguationData":[OSD([sQuery(id+"F2.wireOp",EDGE,"E2.top"),sQuery(id+"F2.wireOp",EDGE,"E2.right")])]});
            var Q2;
            Q2=makeQuery(id+"F3.opExtrude","SWEPT_EDGE",EDGE,{"disambiguationData":[OSD([sQuery(id+"F2.wireOp",EDGE,"E2.bottom"),sQuery(id+"F2.wireOp",EDGE,"E2.left")])]});
            var Q3;
            Q3=makeQuery(id+"F3.opExtrude","SWEPT_EDGE",EDGE,{"disambiguationData":[OSD([sQuery(id+"F2.wireOp",EDGE,"E2.bottom"),sQuery(id+"F2.wireOp",EDGE,"E2.right")])]});
            chamfer(context, id + "F23", {"entities" : qUnion([Q0, Q1, Q2, Q3]), "width" : 15 * mm, "tangentPropagation" : true});
        }
        {
            var Q0;
            Q0=makeQuery(id+"F3.opExtrude","CAP_FACE",FACE,{"disambiguationData":[OSD([sQuery(id+"F2.wireOp",EDGE,"E1.bottom"),sQuery(id+"F2.wireOp",EDGE,"E1.top"),sQuery(id+"F2.wireOp",EDGE,"E1.left"),sQuery(id+"F2.wireOp",EDGE,"E1.right"),sQuery(id+"F2.wireOp",EDGE,"E2.bottom"),sQuery(id+"F2.wireOp",EDGE,"E2.top"),sQuery(id+"F2.wireOp",EDGE,"E2.left"),sQuery(id+"F2.wireOp",EDGE,"E2.right")])],"isStart":false});
            var sketch = newSketch(context, id + "F24", { "sketchPlane" : qUnion([Q0])});
            skLineSegment(sketch, "E54.bottom", {"start": v(-323.37, -260.88) * mm, "end": v(-447.37, -260.88) * mm, "construction": true});
            skLineSegment(sketch, "E54.top", {"start": v(-323.37, 89.12) * mm, "end": v(-447.37, 89.12) * mm, "construction": true});
            skLineSegment(sketch, "E54.left", {"start": v(-323.37, -260.88) * mm, "end": v(-323.37, 89.12) * mm, "construction": true});
            skLineSegment(sketch, "E54.right", {"start": v(-447.37, -260.88) * mm, "end": v(-447.37, 89.12) * mm, "construction": true});
            skPoint(sketch, "E54.middle", {"position": v(-385.37, -85.88) * mm});
            skPoint(sketch, "E54.middle.positionSnap0", {"position": v(-385.37, 96.62) * mm});
            skPoint(sketch, "E54.middle.positionSnap1", {"position": v(-450.87, -85.88) * mm});
            skPoint(sketch, "E54.centerSnap0", {"position": v(-385.37, 96.62) * mm});
            skPoint(sketch, "E54.centerSnap1", {"position": v(-450.87, -85.88) * mm});
            skCircle(sketch, "E55", {"center": v(-447.37, -260.88) * mm, "radius": 1.5 * mm});
            skCircle(sketch, "E56", {"center": v(-323.37, -260.88) * mm, "radius": 1.6 * mm});
            skCircle(sketch, "E57", {"center": v(-323.37, 89.12) * mm, "radius": 1.6 * mm});
            skCircle(sketch, "E58", {"center": v(-447.37, 89.12) * mm, "radius": 1.6 * mm});
            skSolve(sketch);
        }
        {
            var Q0;
            Q0 = qSketchRegion(id + "F24", true);
            extrude(context, id + "F25", {"entities" : qUnion([Q0]), "operationType" : NewBodyOperationType.REMOVE, "oppositeDirection" : true, "depth" : 25 * mm, "offsetDistance" : 25 * mm});
        }
        {
            var Q0;
            Q0=makeQuery(id+"F3.opExtrude","CAP_FACE",FACE,{"disambiguationData":[OSD([sQuery(id+"F2.wireOp",EDGE,"E1.bottom"),sQuery(id+"F2.wireOp",EDGE,"E1.top"),sQuery(id+"F2.wireOp",EDGE,"E1.left"),sQuery(id+"F2.wireOp",EDGE,"E1.right"),sQuery(id+"F2.wireOp",EDGE,"E2.bottom"),sQuery(id+"F2.wireOp",EDGE,"E2.top"),sQuery(id+"F2.wireOp",EDGE,"E2.left"),sQuery(id+"F2.wireOp",EDGE,"E2.right")])],"isStart":false});
            var sketch = newSketch(context, id + "F26", { "sketchPlane" : qUnion([Q0])});
            skLineSegment(sketch, "E59.bottom", {"start": v(-450.87, -101.84) * mm, "end": v(-443.87, -101.84) * mm});
            skLineSegment(sketch, "E59.top", {"start": v(-450.87, -121.84) * mm, "end": v(-443.87, -121.84) * mm});
            skLineSegment(sketch, "E59.left", {"start": v(-450.87, -101.84) * mm, "end": v(-450.87, -121.84) * mm});
            skLineSegment(sketch, "E59.right", {"start": v(-319.87, -101.84) * mm, "end": v(-319.87, -121.84) * mm});
            skLineSegment(sketch, "E60.right", {"start": v(-443.87, -101.84) * mm, "end": v(-443.87, -121.84) * mm});
            skLineSegment(sketch, "E61.bottom", {"start": v(-319.87, -101.84) * mm, "end": v(-326.87, -101.84) * mm});
            skLineSegment(sketch, "E61.top", {"start": v(-319.87, -121.84) * mm, "end": v(-326.87, -121.84) * mm});
            skLineSegment(sketch, "E61.right", {"start": v(-326.87, -101.84) * mm, "end": v(-326.87, -121.84) * mm});
            skLineSegment(sketch, "E62.trimOffspring", {"start": v(-326.87, -101.84) * mm, "end": v(-319.87, -101.84) * mm});
            skLineSegment(sketch, "E63.trimOffspring", {"start": v(-326.87, -121.84) * mm, "end": v(-319.87, -121.84) * mm});
            skCircle(sketch, "E64", {"center": v(-447.37, -111.84) * mm, "radius": 1.6 * mm});
            skPoint(sketch, "E64.centerSnap0", {"position": v(-447.37, -101.84) * mm});
            skPoint(sketch, "E64.centerSnap1", {"position": v(-443.87, -111.84) * mm});
            skCircle(sketch, "E65", {"center": v(-323.37, -111.84) * mm, "radius": 1.6 * mm});
            skPoint(sketch, "E65.centerSnap0", {"position": v(-323.37, -101.84) * mm});
            skPoint(sketch, "E65.centerSnap1", {"position": v(-326.87, -111.84) * mm});
            skSolve(sketch);
        }
        {
            var Q0;
            Q0 = qSketchRegion(id + "F26", true);
            extrude(context, id + "F27", {"entities" : qUnion([Q0]), "operationType" : NewBodyOperationType.ADD, "oppositeDirection" : true, "depth" : 36 * mm, "offsetDistance" : 25 * mm});
        }
        {
            var Q0;
            Q0=makeQuery(id+"F27.opExtrude","SWEPT_EDGE",EDGE,{"disambiguationData":[OSD([sQuery(id+"F26.wireOp",EDGE,"E59.bottom"),sQuery(id+"F26.wireOp",EDGE,"E60.right")])]});
            var Q1;
            Q1=makeQuery(id+"F27.opExtrude","SWEPT_EDGE",EDGE,{"disambiguationData":[OSD([sQuery(id+"F26.wireOp",EDGE,"E59.top"),sQuery(id+"F26.wireOp",EDGE,"E60.right")])]});
            var Q2;
            Q2=makeQuery(id+"F27.opExtrude","SWEPT_EDGE",EDGE,{"disambiguationData":[OSD([sQuery(id+"F26.wireOp",EDGE,"E61.right"),sQuery(id+"F26.wireOp",EDGE,"E63.trimOffspring")])]});
            var Q3;
            Q3=makeQuery(id+"F27.opExtrude","SWEPT_EDGE",EDGE,{"disambiguationData":[OSD([sQuery(id+"F26.wireOp",EDGE,"E61.right"),sQuery(id+"F26.wireOp",EDGE,"E62.trimOffspring")])]});
            chamfer(context, id + "F28", {"entities" : qUnion([Q0, Q1, Q2, Q3]), "width" : 8 * mm, "tangentPropagation" : true});
        }
        {
            var Q0;
            Q0=qCreatedBy(makeId("Top.planeOp"),FACE);
            var sketch = newSketch(context, id + "F29", { "sketchPlane" : qUnion([Q0])});
            skCircle(sketch, "E66", {"center": v(-777.05, 89.1) * mm, "radius": 2 * mm});
            skCircle(sketch, "E67", {"center": v(-653.05, 89.1) * mm, "radius": 2 * mm});
            skCircle(sketch, "E68", {"center": v(-653.05, -111.87) * mm, "radius": 2 * mm});
            skCircle(sketch, "E69", {"center": v(-653.05, -260.9) * mm, "radius": 2 * mm});
            skCircle(sketch, "E70", {"center": v(-777.05, -260.9) * mm, "radius": 2 * mm});
            skCircle(sketch, "E71", {"center": v(-777.05, -111.87) * mm, "radius": 2 * mm});
            skLineSegment(sketch, "E72.bottom", {"start": v(-783.05, 96.6) * mm, "end": v(-647.05, 96.6) * mm, "construction": true});
            skLineSegment(sketch, "E72.left", {"start": v(-783.05, 96.6) * mm, "end": v(-783.05, -102.87) * mm, "construction": true});
            skLineSegment(sketch, "E72.right", {"start": v(-647.05, 96.6) * mm, "end": v(-647.05, -102.87) * mm, "construction": true});
            skLineSegment(sketch, "E73", {"start": v(-715.05, 96.6) * mm, "end": v(-715.05, 86.6) * mm, "construction": true});
            skLineSegment(sketch, "E74", {"start": v(-783.05, -85.9) * mm, "end": v(-771.05, -85.9) * mm, "construction": true});
            skLineSegment(sketch, "E75.bottom", {"start": v(-773.05, 86.6) * mm, "end": v(-657.05, 86.6) * mm, "construction": true});
            skLineSegment(sketch, "E75.left", {"start": v(-773.05, 86.6) * mm, "end": v(-773.05, -102.87) * mm, "construction": true});
            skLineSegment(sketch, "E75.right", {"start": v(-657.05, 86.6) * mm, "end": v(-657.05, -102.87) * mm, "construction": true});
            skPoint(sketch, "E75.middle", {"position": v(-715.05, -85.9) * mm});
            skLineSegment(sketch, "E76", {"start": v(-773.05, -102.87) * mm, "end": v(-657.05, -102.87) * mm, "construction": true});
            skLineSegment(sketch, "E77", {"start": v(-783.05, 96.6) * mm, "end": v(-783.05, 111.6) * mm, "construction": true});
            skLineSegment(sketch, "E78", {"start": v(-783.05, 96.6) * mm, "end": v(-798.05, 96.6) * mm, "construction": true});
            skLineSegment(sketch, "E79", {"start": v(-647.05, -268.4) * mm, "end": v(-647.05, -283.4) * mm, "construction": true});
            skLineSegment(sketch, "E80", {"start": v(-647.05, -268.4) * mm, "end": v(-632.05, -268.4) * mm, "construction": true});
            skLineSegment(sketch, "E81.bottom", {"start": v(-798.05, 111.6) * mm, "end": v(-632.05, 111.6) * mm});
            skLineSegment(sketch, "E81.top", {"start": v(-798.05, -283.4) * mm, "end": v(-632.05, -283.4) * mm});
            skLineSegment(sketch, "E81.left", {"start": v(-798.05, 111.6) * mm, "end": v(-798.05, -283.4) * mm});
            skLineSegment(sketch, "E81.right", {"start": v(-632.05, 111.6) * mm, "end": v(-632.05, -283.4) * mm});
            skLineSegment(sketch, "E82", {"start": v(-657.05, -102.87) * mm, "end": v(-632.05, -102.87) * mm, "construction": true});
            skLineSegment(sketch, "E83", {"start": v(-632.05, -102.87) * mm, "end": v(-798.05, -102.87) * mm, "construction": true});
            skLineSegment(sketch, "E84", {"start": v(-653.05, -6.89) * mm, "end": v(-823.46, -6.89) * mm, "construction": true});
            skLineSegment(sketch, "E85", {"start": v(-823.46, -6.89) * mm, "end": v(-604.59, -6.89) * mm, "construction": true});
            skLineSegment(sketch, "E86", {"start": v(-653.05, 41.1) * mm, "end": v(-702.7, 41.1) * mm, "construction": true});
            skLineSegment(sketch, "E87", {"start": v(-773.05, -102.87) * mm, "end": v(-657.05, -102.87) * mm});
            skLineSegment(sketch, "E88", {"start": v(-653.05, 41.1) * mm, "end": v(-653.05, 51.1) * mm, "construction": true});
            skLineSegment(sketch, "E89", {"start": v(-653.05, 51.1) * mm, "end": v(-653.05, 31.1) * mm, "construction": true});
            skCircle(sketch, "E90", {"center": v(-653.05, 51.1) * mm, "radius": 2 * mm});
            skCircle(sketch, "E91", {"center": v(-653.05, 31.1) * mm, "radius": 2 * mm});
            skCircle(sketch, "E92.MirrorC", {"center": v(-653.05, -44.88) * mm, "radius": 2 * mm});
            skCircle(sketch, "E93.MirrorC", {"center": v(-653.05, -64.88) * mm, "radius": 2 * mm});
            skLineSegment(sketch, "E94", {"start": v(-777.05, -6.89) * mm, "end": v(-777.05, 3.11) * mm, "construction": true});
            skLineSegment(sketch, "E95", {"start": v(-777.05, 3.11) * mm, "end": v(-777.05, -16.89) * mm, "construction": true});
            skCircle(sketch, "E96", {"center": v(-777.05, 3.11) * mm, "radius": 2 * mm});
            skCircle(sketch, "E97", {"center": v(-777.05, -16.89) * mm, "radius": 2 * mm});
            skLineSegment(sketch, "E98", {"start": v(-777.05, -111.87) * mm, "end": v(-653.05, -111.87) * mm, "construction": true});
            skLineSegment(sketch, "E99", {"start": v(-653.05, -111.87) * mm, "end": v(-653.05, -260.9) * mm, "construction": true});
            skLineSegment(sketch, "E100.bottom", {"start": v(-750.8, -150.64) * mm, "end": v(-679.3, -150.64) * mm, "construction": true});
            skLineSegment(sketch, "E100.top", {"start": v(-750.8, -222.14) * mm, "end": v(-679.3, -222.14) * mm, "construction": true});
            skLineSegment(sketch, "E100.left", {"start": v(-750.8, -150.64) * mm, "end": v(-750.8, -222.14) * mm, "construction": true});
            skLineSegment(sketch, "E100.right", {"start": v(-679.3, -150.64) * mm, "end": v(-679.3, -222.14) * mm, "construction": true});
            skPoint(sketch, "E100.middle", {"position": v(-715.05, -186.39) * mm});
            skPoint(sketch, "E100.middle.positionSnap0", {"position": v(-653.05, -186.39) * mm});
            skPoint(sketch, "E100.middle.positionSnap1", {"position": v(-715.05, -111.87) * mm});
            skPoint(sketch, "E100.centerSnap0", {"position": v(-653.05, -186.39) * mm});
            skPoint(sketch, "E100.centerSnap1", {"position": v(-715.05, -111.87) * mm});
            skCircle(sketch, "E101", {"center": v(-750.8, -150.64) * mm, "radius": 2 * mm});
            skCircle(sketch, "E102", {"center": v(-679.3, -150.64) * mm, "radius": 2 * mm});
            skCircle(sketch, "E103", {"center": v(-679.3, -222.14) * mm, "radius": 2 * mm});
            skCircle(sketch, "E104", {"center": v(-750.8, -222.14) * mm, "radius": 2 * mm});
            skArc(sketch, "E105", {"start": v(-716.5, -150.67) * mm, "mid": v(-715.4, -222.13) * mm, "end": v(-712.9, -150.7) * mm});
            skLineSegment(sketch, "E106.bottom", {"start": v(-659.05, -99.39) * mm, "end": v(-771.05, -99.39) * mm});
            skLineSegment(sketch, "E106.top", {"start": v(-659.05, 85.61) * mm, "end": v(-711.12, 85.61) * mm});
            skLineSegment(sketch, "E106.left", {"start": v(-659.05, -99.39) * mm, "end": v(-659.05, 85.61) * mm});
            skLineSegment(sketch, "E106.right", {"start": v(-771.05, -99.39) * mm, "end": v(-771.05, 85.61) * mm});
            skPoint(sketch, "E106.middle", {"position": v(-715.05, -6.89) * mm});
            skCircle(sketch, "E107", {"center": v(-697.15, -234.72) * mm, "radius": 4 * mm});
            skLineSegment(sketch, "E108.bottom", {"start": v(-662.55, 82.11) * mm, "end": v(-711.12, 82.11) * mm});
            skLineSegment(sketch, "E108.top", {"start": v(-662.55, -95.89) * mm, "end": v(-767.55, -95.89) * mm});
            skLineSegment(sketch, "E108.left", {"start": v(-662.55, 82.11) * mm, "end": v(-662.55, -95.89) * mm});
            skLineSegment(sketch, "E108.right", {"start": v(-767.55, 82.11) * mm, "end": v(-767.55, -95.89) * mm});
            skLineSegment(sketch, "E109", {"start": v(-717.73, 82.11) * mm, "end": v(-717.73, 85.61) * mm});
            skLineSegment(sketch, "E110", {"start": v(-711.12, 82.11) * mm, "end": v(-711.12, 85.61) * mm});
            skLineSegment(sketch, "E111.trimOffspring", {"start": v(-717.73, 82.11) * mm, "end": v(-767.55, 82.11) * mm});
            skLineSegment(sketch, "E112.trimOffspring", {"start": v(-717.73, 85.61) * mm, "end": v(-771.05, 85.61) * mm});
            skArc(sketch, "E113", {"start": v(-716.5, -154.42) * mm, "mid": v(-715.4, -218.38) * mm, "end": v(-712.9, -154.46) * mm});
            skLineSegment(sketch, "E114", {"start": v(-716.5, -154.42) * mm, "end": v(-716.5, -150.67) * mm});
            skLineSegment(sketch, "E115", {"start": v(-712.9, -154.46) * mm, "end": v(-712.9, -150.7) * mm});
            skSolve(sketch);
        }
        {
            var Q0;
            Q0 = qSketchRegion(id + "F29", true);
            extrude(context, id + "F30", {"entities" : qUnion([Q0]), "depth" : 3 * mm, "offsetDistance" : 25 * mm});
        }
        {
            var Q0;
            Q0=qCreatedBy(makeId("Top.planeOp"),FACE);
            var sketch = newSketch(context, id + "F31", { "sketchPlane" : qUnion([Q0])});
            skLineSegment(sketch, "E116.bottom", {"start": v(-1205.05, 88.03) * mm, "end": v(-1039.05, 88.03) * mm});
            skLineSegment(sketch, "E116.top", {"start": v(-1205.05, -147.16) * mm, "end": v(-1039.05, -147.16) * mm});
            skLineSegment(sketch, "E116.left", {"start": v(-1205.05, 88.03) * mm, "end": v(-1205.05, -147.16) * mm});
            skLineSegment(sketch, "E116.right", {"start": v(-1039.05, 88.03) * mm, "end": v(-1039.05, -147.16) * mm});
            skCircle(sketch, "E117", {"center": v(-1184.05, 65.53) * mm, "radius": 2 * mm});
            skCircle(sketch, "E118", {"center": v(-1060.05, 65.53) * mm, "radius": 2 * mm});
            skCircle(sketch, "E119", {"center": v(-1060.05, 27.54) * mm, "radius": 2 * mm});
            skCircle(sketch, "E120", {"center": v(-1060.05, 7.54) * mm, "radius": 2 * mm});
            skCircle(sketch, "E121", {"center": v(-1060.05, -68.45) * mm, "radius": 2 * mm});
            skCircle(sketch, "E122", {"center": v(-1060.05, -88.45) * mm, "radius": 2 * mm});
            skCircle(sketch, "E123", {"center": v(-1060.05, -135.44) * mm, "radius": 2 * mm});
            skCircle(sketch, "E124", {"center": v(-1184.05, -135.44) * mm, "radius": 2 * mm});
            skCircle(sketch, "E125", {"center": v(-1184.05, -20.45) * mm, "radius": 2 * mm});
            skCircle(sketch, "E126", {"center": v(-1184.05, -40.45) * mm, "radius": 2 * mm});
            skLineSegment(sketch, "E127.bottom", {"start": v(-1180.05, 63.03) * mm, "end": v(-1064.05, 63.03) * mm});
            skLineSegment(sketch, "E127.top", {"start": v(-1180.05, -126.44) * mm, "end": v(-1064.05, -126.44) * mm});
            skLineSegment(sketch, "E127.left", {"start": v(-1180.05, 63.03) * mm, "end": v(-1180.05, -126.44) * mm});
            skLineSegment(sketch, "E127.right", {"start": v(-1064.05, 63.03) * mm, "end": v(-1064.05, -126.44) * mm});
            skSolve(sketch);
        }
        {
            var Q0;
            Q0 = qSketchRegion(id + "F31", true);
            extrude(context, id + "F32", {"entities" : qUnion([Q0]), "depth" : 3 * mm, "offsetDistance" : 25 * mm});
        }
        {
            var Q0;
            Q0=qCreatedBy(makeId("Top.planeOp"),FACE);
            var sketch = newSketch(context, id + "F33", { "sketchPlane" : qUnion([Q0])});
            skLineSegment(sketch, "E128.bottom", {"start": v(389.25, -5.05) * mm, "end": v(460.75, -5.05) * mm, "construction": true});
            skLineSegment(sketch, "E128.top", {"start": v(389.25, -76.55) * mm, "end": v(460.75, -76.55) * mm, "construction": true});
            skLineSegment(sketch, "E128.left", {"start": v(389.25, -5.05) * mm, "end": v(389.25, -76.55) * mm, "construction": true});
            skLineSegment(sketch, "E128.right", {"start": v(460.75, -5.05) * mm, "end": v(460.75, -76.55) * mm, "construction": true});
            skCircle(sketch, "E129", {"center": v(389.25, -5.05) * mm, "radius": 1.75 * mm});
            skCircle(sketch, "E130", {"center": v(460.75, -5.05) * mm, "radius": 1.75 * mm});
            skCircle(sketch, "E131", {"center": v(460.75, -76.55) * mm, "radius": 1.75 * mm});
            skCircle(sketch, "E132", {"center": v(389.25, -76.55) * mm, "radius": 1.75 * mm});
            skLineSegment(sketch, "E133.bottom", {"start": v(465, -80.8) * mm, "end": v(385, -80.8) * mm});
            skLineSegment(sketch, "E133.top", {"start": v(465, -0.8) * mm, "end": v(385, -0.8) * mm});
            skLineSegment(sketch, "E133.left", {"start": v(465, -80.8) * mm, "end": v(465, -0.8) * mm});
            skLineSegment(sketch, "E133.right", {"start": v(385, -80.8) * mm, "end": v(385, -0.8) * mm});
            skPoint(sketch, "E133.middle", {"position": v(425, -40.8) * mm});
            skPoint(sketch, "E133.middle.positionSnap0", {"position": v(389.25, -40.8) * mm});
            skPoint(sketch, "E133.middle.positionSnap1", {"position": v(425, -5.05) * mm});
            skPoint(sketch, "E133.centerSnap0", {"position": v(389.25, -40.8) * mm});
            skPoint(sketch, "E133.centerSnap1", {"position": v(425, -5.05) * mm});
            skCircle(sketch, "E134", {"center": v(425, -40.8) * mm, "radius": 36.5 * mm});
            skSolve(sketch);
        }
        {
            var Q0;
            Q0 = qSketchRegion(id + "F33", true);
            extrude(context, id + "F34", {"entities" : qUnion([Q0]), "depth" : 3 * mm, "offsetDistance" : 25 * mm});
        }
        {
            var Q0;
            Q0=makeQuery(id+"F34.opExtrude","CAP_FACE",FACE,{"disambiguationData":[OSD([sQuery(id+"F33.wireOp",EDGE,"E129"),sQuery(id+"F33.wireOp",EDGE,"E130"),sQuery(id+"F33.wireOp",EDGE,"E131"),sQuery(id+"F33.wireOp",EDGE,"E132"),sQuery(id+"F33.wireOp",EDGE,"E133.bottom"),sQuery(id+"F33.wireOp",EDGE,"E133.top"),sQuery(id+"F33.wireOp",EDGE,"E133.left"),sQuery(id+"F33.wireOp",EDGE,"E133.right"),sQuery(id+"F33.wireOp",EDGE,"E134")])],"isStart":false});
            var sketch = newSketch(context, id + "F35", { "sketchPlane" : qUnion([Q0])});
            skCircle(sketch, "E135", {"center": v(425, -40.8) * mm, "radius": 40 * mm});
            skCircle(sketch, "E136", {"center": v(425, -40.8) * mm, "radius": 36.5 * mm});
            skSolve(sketch);
        }
        {
            var Q0;
            Q0 = qSketchRegion(id + "F35", true);
            extrude(context, id + "F36", {"entities" : qUnion([Q0]), "operationType" : NewBodyOperationType.ADD, "depth" : 10 * mm, "offsetDistance" : 25 * mm});
        }
        {
            var Q0;
            Q0=makeQuery(id+"F36.opExtrude","CAP_FACE",FACE,{"disambiguationData":[OSD([sQuery(id+"F35.wireOp",EDGE,"E135"),sQuery(id+"F35.wireOp",EDGE,"E136")])],"isStart":false});
            var sketch = newSketch(context, id + "F37", { "sketchPlane" : qUnion([Q0])});
            skLineSegment(sketch, "E137.bottom", {"start": v(464.97, -42.3) * mm, "end": v(428.62, -42.3) * mm});
            skLineSegment(sketch, "E137.top", {"start": v(464.97, -39.3) * mm, "end": v(428.62, -39.3) * mm});
            skLineSegment(sketch, "E137.left", {"start": v(464.97, -42.3) * mm, "end": v(464.97, -39.3) * mm});
            skLineSegment(sketch, "E137.right", {"start": v(385.03, -42.3) * mm, "end": v(385.03, -39.3) * mm});
            skPoint(sketch, "E137.middle", {"position": v(425, -40.8) * mm});
            skLineSegment(sketch, "E138.bottom", {"start": v(426.5, -0.82) * mm, "end": v(423.5, -0.82) * mm});
            skLineSegment(sketch, "E138.top", {"start": v(426.5, -80.77) * mm, "end": v(423.5, -80.77) * mm});
            skLineSegment(sketch, "E138.left", {"start": v(426.5, -0.82) * mm, "end": v(426.5, -37.18) * mm});
            skLineSegment(sketch, "E138.right", {"start": v(423.5, -0.82) * mm, "end": v(423.5, -37.18) * mm});
            skLineSegment(sketch, "E139", {"start": v(408.92, -26.84) * mm, "end": v(421.38, -39.3) * mm});
            skLineSegment(sketch, "E140", {"start": v(411.04, -24.72) * mm, "end": v(423.5, -37.18) * mm});
            skLineSegment(sketch, "E141", {"start": v(408.92, -26.84) * mm, "end": v(395.67, -13.6) * mm});
            skLineSegment(sketch, "E142", {"start": v(411.04, -24.72) * mm, "end": v(397.8, -11.47) * mm});
            skLineSegment(sketch, "E143", {"start": v(395.67, -13.6) * mm, "end": v(397.8, -11.47) * mm});
            skLineSegment(sketch, "E144.MirrorCS", {"start": v(454.32, -13.6) * mm, "end": v(452.2, -11.47) * mm});
            skLineSegment(sketch, "E145.MirrorCS", {"start": v(454.32, -68) * mm, "end": v(452.2, -70.12) * mm});
            skLineSegment(sketch, "E146.MirrorCS", {"start": v(395.67, -68) * mm, "end": v(397.8, -70.12) * mm});
            skLineSegment(sketch, "E147", {"start": v(426.5, -37.18) * mm, "end": v(452.2, -11.47) * mm});
            skLineSegment(sketch, "E148", {"start": v(428.62, -39.3) * mm, "end": v(454.32, -13.6) * mm});
            skLineSegment(sketch, "E149", {"start": v(421.38, -42.3) * mm, "end": v(395.67, -68) * mm});
            skLineSegment(sketch, "E150", {"start": v(423.5, -44.42) * mm, "end": v(397.8, -70.12) * mm});
            skLineSegment(sketch, "E151", {"start": v(426.5, -44.42) * mm, "end": v(452.2, -70.12) * mm});
            skLineSegment(sketch, "E152", {"start": v(428.62, -42.3) * mm, "end": v(454.32, -68) * mm});
            skLineSegment(sketch, "E153.trimOffspring", {"start": v(423.5, -44.42) * mm, "end": v(423.5, -80.77) * mm});
            skLineSegment(sketch, "E154.trimOffspring", {"start": v(426.5, -44.42) * mm, "end": v(426.5, -80.77) * mm});
            skLineSegment(sketch, "E155.trimOffspring", {"start": v(421.38, -39.3) * mm, "end": v(385.03, -39.3) * mm});
            skLineSegment(sketch, "E156.trimOffspring", {"start": v(421.38, -42.3) * mm, "end": v(385.03, -42.3) * mm});
            skSolve(sketch);
        }
        {
            var Q0;
            Q0 = qSketchRegion(id + "F37", true);
            extrude(context, id + "F38", {"entities" : qUnion([Q0]), "operationType" : NewBodyOperationType.ADD, "oppositeDirection" : true, "depth" : 3 * mm, "offsetDistance" : 25 * mm});
        }
        {
            var Q0;
            {var subQ0=sQuery(id+"F33.wireOp",EDGE,"E133.left");var subQ1=sQuery(id+"F33.wireOp",EDGE,"E133.bottom");var subQ2=sQuery(id+"F35.wireOp",EDGE,"E135");Q0=makeQuery(id+"F36.boolean.opBoolean","SPLIT",EDGE,{"disambiguationData":[TD([makeQuery(id+"F34.opExtrude","CAP_FACE",FACE,{"disambiguationData":[OSD([sQuery(id+"F33.wireOp",EDGE,"E129"),sQuery(id+"F33.wireOp",EDGE,"E130"),sQuery(id+"F33.wireOp",EDGE,"E131"),sQuery(id+"F33.wireOp",EDGE,"E132"),subQ1,sQuery(id+"F33.wireOp",EDGE,"E133.top"),subQ0,sQuery(id+"F33.wireOp",EDGE,"E133.right"),sQuery(id+"F33.wireOp",EDGE,"E134")])],"isStart":false}),makeQuery(id+"F34.opExtrude","SWEPT_FACE",FACE,{"disambiguationData":[OSD([subQ1])]}),makeQuery(id+"F34.opExtrude","SWEPT_FACE",FACE,{"disambiguationData":[OSD([subQ0])]}),makeQuery(id+"F36.opExtrude","SWEPT_FACE",FACE,{"disambiguationData":[OSD([subQ2])]})])],"derivedFrom":makeQuery(id+"F36.opExtrude","CAP_EDGE",EDGE,{"disambiguationData":[OSD([subQ2])],"isStart":true})});}
            chamfer(context, id + "F39", {"entities" : qUnion([Q0]), "width" : 5 * mm, "tangentPropagation" : true});
        }
        {
            var Q0;
            Q0=makeQuery(id+"F38.boolean.opBoolean","MERGE",FACE,{"derivedFrom":[makeQuery(id+"F36.opExtrude","CAP_FACE",FACE,{"disambiguationData":[OSD([sQuery(id+"F35.wireOp",EDGE,"E135"),sQuery(id+"F35.wireOp",EDGE,"E136")])],"isStart":false}),makeQuery(id+"F38.opExtrude","CAP_FACE",FACE,{"disambiguationData":[OSD([sQuery(id+"F37.wireOp",EDGE,"E137.bottom"),sQuery(id+"F37.wireOp",EDGE,"E137.top"),sQuery(id+"F37.wireOp",EDGE,"E137.left"),sQuery(id+"F37.wireOp",EDGE,"E137.right"),sQuery(id+"F37.wireOp",EDGE,"E138.bottom"),sQuery(id+"F37.wireOp",EDGE,"E138.top"),sQuery(id+"F37.wireOp",EDGE,"E138.left"),sQuery(id+"F37.wireOp",EDGE,"E138.right"),sQuery(id+"F37.wireOp",EDGE,"E139"),sQuery(id+"F37.wireOp",EDGE,"E140"),sQuery(id+"F37.wireOp",EDGE,"E141"),sQuery(id+"F37.wireOp",EDGE,"E142"),sQuery(id+"F37.wireOp",EDGE,"E143"),sQuery(id+"F37.wireOp",EDGE,"E144.MirrorCS"),sQuery(id+"F37.wireOp",EDGE,"E145.MirrorCS"),sQuery(id+"F37.wireOp",EDGE,"E146.MirrorCS"),sQuery(id+"F37.wireOp",EDGE,"E147"),sQuery(id+"F37.wireOp",EDGE,"E148"),sQuery(id+"F37.wireOp",EDGE,"E149"),sQuery(id+"F37.wireOp",EDGE,"E150"),sQuery(id+"F37.wireOp",EDGE,"E151"),sQuery(id+"F37.wireOp",EDGE,"E152"),sQuery(id+"F37.wireOp",EDGE,"E153.trimOffspring"),sQuery(id+"F37.wireOp",EDGE,"E154.trimOffspring"),sQuery(id+"F37.wireOp",EDGE,"E155.trimOffspring"),sQuery(id+"F37.wireOp",EDGE,"E156.trimOffspring")])],"isStart":true})]});
            fillet(context, id + "F40", {"entities" : qUnion([Q0]), "radius" : 1.5 * mm, "tangentPropagation" : true, "allowEdgeOverflow" : false});
        }
        {
            var Q0;
            Q0=makeQuery(id+"F34.opExtrude","CAP_EDGE",EDGE,{"disambiguationData":[OSD([sQuery(id+"F33.wireOp",EDGE,"E134")])],"isStart":true});
            fillet(context, id + "F41", {"entities" : qUnion([Q0]), "radius" : 2 * mm, "tangentPropagation" : true, "allowEdgeOverflow" : false});
        }
        {
            var Q0;
            Q0=makeQuery(id+"F34.opExtrude","SWEPT_EDGE",EDGE,{"disambiguationData":[OSD([sQuery(id+"F33.wireOp",EDGE,"E133.top"),sQuery(id+"F33.wireOp",EDGE,"E133.left")])]});
            var Q1;
            Q1=makeQuery(id+"F34.opExtrude","SWEPT_EDGE",EDGE,{"disambiguationData":[OSD([sQuery(id+"F33.wireOp",EDGE,"E133.top"),sQuery(id+"F33.wireOp",EDGE,"E133.right")])]});
            var Q2;
            Q2=makeQuery(id+"F34.opExtrude","SWEPT_EDGE",EDGE,{"disambiguationData":[OSD([sQuery(id+"F33.wireOp",EDGE,"E133.bottom"),sQuery(id+"F33.wireOp",EDGE,"E133.right")])]});
            var Q3;
            Q3=makeQuery(id+"F34.opExtrude","SWEPT_EDGE",EDGE,{"disambiguationData":[OSD([sQuery(id+"F33.wireOp",EDGE,"E133.bottom"),sQuery(id+"F33.wireOp",EDGE,"E133.left")])]});
            fillet(context, id + "F42", {"entities" : qUnion([Q0, Q1, Q2, Q3]), "radius" : 5 * mm, "tangentPropagation" : true, "allowEdgeOverflow" : false});
        }
    });
